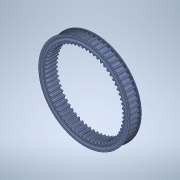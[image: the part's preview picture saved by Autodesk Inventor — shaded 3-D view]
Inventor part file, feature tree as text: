
AUTODESK INVENTOR PART (.ipt)
format: ipt  version: 2020 (Build 240168000, 168)  size: 1,275,392 bytes
history: native  units: mm (DEFAULTED — no unit token found)
features: sketch x5, extrude x4, plane x4, other x3, revolve x1, chamfer x1, mirror x1
ambient origin geometry x8: Origin, YZ Plane, XZ Plane, XY Plane, X Axis, Y Axis, Z Axis, Center Point
bodies: Solid1 (feature_tree)
feature tree (19):
  extrude  "Extrusion1"  Depth=12.065mm TaperAngle=0.0deg
  plane  "Work Plane1"
  plane  "Work Plane2"
  plane  "Work Plane3"
  other  "Spur Gear"
  sketch  "Sketch3"  dims[d6=0.0mm d7=0.490874mm d9=0.0mm]
  extrude  "Extrusion2"  Depth=76.2mm TaperAngle=0.0deg
  extrude  "Extrusion3"  TaperAngle=0.0deg  [1 undecoded]
  extrude  "Extrusion6"  TaperAngle=0.0deg  [1 undecoded]
  revolve  "Revolution1"  [1 undecoded]
  plane  "Work Plane4"
  chamfer  "Chamfer1"  Distance=90.19mm
  mirror  "Mirror1"
  sketch  "Sketch1"  dims[d0=92.9005mm d1=12.065mm d2=0.0mm]
  sketch  "Sketch2"  dims[d3=81.28mm d4=76.2mm d5=0.0mm]
  other  "Srf1"
  sketch  "Sketch4"  dims[d14=0.0mm d15=30.48mm d16=0.0mm]
  sketch  "Sketch6"  dims[d17=0.0mm d18=0.0mm d19=30.48mm d20=94.35mm d21=90.19mm d23=1.047198mm d24=3.05mm d26=600.0mm d28=360.0deg d30=25.4mm d31=0.0mm d32=25.4mm d33=0.0mm d34=0.01mm d35=0.01mm d38=0.8mm d43=1.0mm d44=0.0mm d45=3.175mm d46=44.45mm d47=0.508mm d48=90.0deg d49=0.4mm d50=3.175mm d51=45.0deg d52=0.9mm]
  other  "Pitch Diameter"
note: 3 required parameter values undecoded (feature->parameter linkage not recoverable at this tier; creation-order binding heuristic only, values carry confidence <= 0.55)